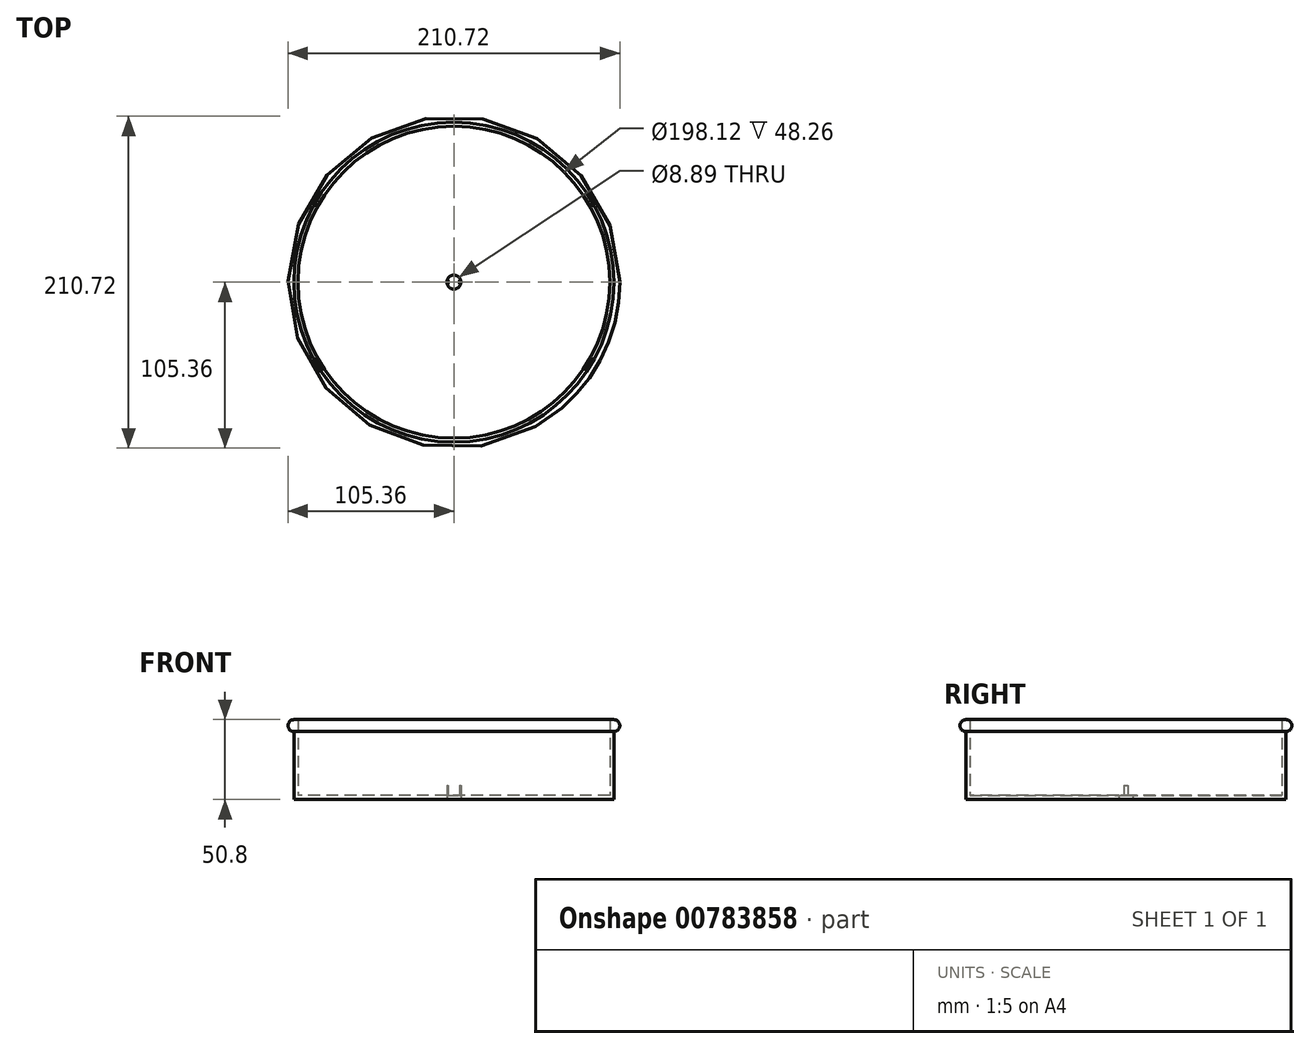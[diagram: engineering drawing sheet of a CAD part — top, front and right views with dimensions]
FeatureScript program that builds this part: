
annotation { "Feature Type Name" : "Feature", "Feature Type Description" : "" }
export const myFeature = defineFeature(function(context is Context, id is Id, definition is map)
    precondition{}
    {
        {
            var Q0;
            Q0=qCreatedBy(makeId("Top.planeOp"),FACE);
            var sketch = newSketch(context, id + "F0", { "sketchPlane" : qUnion([Q0])});
            skCircle(sketch, "E0", {"center": v(0, 0) * mm, "radius": 101.6 * mm});
            skSolve(sketch);
        }
        {
            var Q0;
            Q0=makeQuery(id+"F0.imprint","IMPRINT",FACE,{"disambiguationData":[TD([[makeQuery(id+"F0.imprint","IMPRINT",EDGE,{"derivedFrom":sQuery(id+"F0.wireOp",EDGE,"E0")}),1.0]])]});
            extrude(context, id + "F1", {"entities" : qUnion([Q0]), "depth" : 50.8 * mm, "offsetDistance" : 25.4 * mm});
        }
        {
            var Q0;
            Q0=makeQuery(id+"F1.opExtrude","CAP_FACE",FACE,{"disambiguationData":[OSD([sQuery(id+"F0.wireOp",EDGE,"E0")])],"isStart":false});
            shell(context, id + "F2", {"entities" : qUnion([Q0]), "thickness" : 2.54 * mm});
        }
        {
            var Q0;
            Q0=qCreatedBy(makeId("Front.planeOp"),FACE);
            var sketch = newSketch(context, id + "F3", { "sketchPlane" : qUnion([Q0])});
            skLineSegment(sketch, "E1", {"start": v(0, 50.8) * mm, "end": v(0, 50.8) * mm, "construction": true});
            skLineSegment(sketch, "E2", {"start": v(101.6, 50.8) * mm, "end": v(101.6, 0) * mm, "construction": true});
            skLineSegment(sketch, "E3", {"start": v(-101.6, 0) * mm, "end": v(-101.6, 50.8) * mm, "construction": true});
            skLineSegment(sketch, "E4.0", {"start": v(-101.6, 50.8) * mm, "end": v(101.6, 50.8) * mm, "construction": true});
            skArc(sketch, "E5", {"start": v(101.6, 43.18) * mm, "mid": v(105.36, 47) * mm, "end": v(101.6, 50.8) * mm});
            skLineSegment(sketch, "E6", {"start": v(0, 50.8) * mm, "end": v(0, 0) * mm, "construction": true});
            skLineSegment(sketch, "E7", {"start": v(101.6, 50.8) * mm, "end": v(101.6, 43.18) * mm});
            skSolve(sketch);
        }
        {
            var Q0;
            Q0 = qSketchRegion(id + "F3", true);
            var Q1;
            Q1=sQuery(id+"F3.wireOp",EDGE,"E6");
            revolve(context, id + "F4", {"operationType" : NewBodyOperationType.ADD, "surfaceOperationType" : NewSurfaceOperationType.NEW, "entities" : qUnion([Q0]), "axis" : qUnion([Q1]), "revolveType" : RevolveType.FULL});
        }
        {
            var Q0;
            {var subQ0=sQuery(id+"F0.wireOp",EDGE,"E0");Q0=makeQuery(id+"F2.opShell","OFFSET_FACE",FACE,{"disambiguationData":[OSD([subQ0]),TDD([makeQuery(id+"F1.opExtrude","CAP_FACE",FACE,{"disambiguationData":[OSD([subQ0])],"isStart":true})])]});}
            var sketch = newSketch(context, id + "F5", { "sketchPlane" : qUnion([Q0])});
            skPoint(sketch, "E8", {"position": v(0, 0) * mm});
            skSolve(sketch);
        }
        {
            var Q0;
            Q0=sQuery(id+"F5.wireOp",VERTEX,"E8");
            var Q1;
            Q1=makeQuery(id+"F1.opExtrude","SWEPT_BODY",BODY,{"disambiguationData":[OSD([sQuery(id+"F0.wireOp",EDGE,"E0")])]});
            hole(context, id + "F6", {"style" : HoleStyle.SIMPLE, "endStyle" : HoleEndStyle.THROUGH, "holeDiameter" : 8.9 * mm, "majorDiameter" : 6.35 * mm, "isTappedThrough" : true, "tappedDepth" : 12.7 * mm, "tapClearance" : 3, "locations" : qUnion([Q0]), "scope" : qUnion([Q1]), "startStyle" : HoleStartStyle.PART});
        }
        {
            var Q0;
            {var subQ0=sQuery(id+"F0.wireOp",EDGE,"E0");Q0=makeQuery(id+"F2.opShell","OFFSET_FACE",FACE,{"disambiguationData":[OSD([subQ0]),TDD([makeQuery(id+"F1.opExtrude","CAP_FACE",FACE,{"disambiguationData":[OSD([subQ0])],"isStart":true})])]});}
            var sketch = newSketch(context, id + "F7", { "sketchPlane" : qUnion([Q0])});
            skArc(sketch, "E9", {"start": v(-4.26, 1.27) * mm, "mid": v(-4.45, 0) * mm, "end": v(-4.26, -1.27) * mm});
            skArc(sketch, "E10", {"start": v(4.26, -1.27) * mm, "mid": v(4.45, 0) * mm, "end": v(4.26, 1.27) * mm});
            skArc(sketch, "E11", {"start": v(-3.6, 1.27) * mm, "mid": v(-3.81, 0) * mm, "end": v(-3.6, -1.27) * mm});
            skLineSegment(sketch, "E12", {"start": v(-4.26, 1.27) * mm, "end": v(-3.6, 1.27) * mm});
            skLineSegment(sketch, "E13", {"start": v(-4.26, -1.27) * mm, "end": v(-3.6, -1.27) * mm});
            skArc(sketch, "E14.trimOffspring", {"start": v(3.6, -1.27) * mm, "mid": v(3.8, 0) * mm, "end": v(3.6, 1.27) * mm});
            skLineSegment(sketch, "E15.trimOffspring", {"start": v(3.6, -1.27) * mm, "end": v(4.26, -1.27) * mm});
            skLineSegment(sketch, "E16.trimOffspring", {"start": v(3.6, 1.27) * mm, "end": v(4.26, 1.27) * mm});
            skSolve(sketch);
        }
        {
            var Q0;
            Q0 = qSketchRegion(id + "F7", true);
            extrude(context, id + "F8", {"entities" : qUnion([Q0]), "operationType" : NewBodyOperationType.ADD, "depth" : 6.35 * mm, "offsetDistance" : 25.4 * mm});
        }
    });
